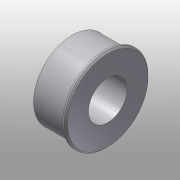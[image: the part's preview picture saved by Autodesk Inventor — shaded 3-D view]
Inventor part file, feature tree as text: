
AUTODESK INVENTOR PART (.ipt)
format: ipt  version: 2016 (Build 200138000, 138)  size: 109,056 bytes
history: native  units: mm
features: extrude x3, sketch x3, chamfer x1
ambient origin geometry x8: Origin, YZ Plane, XZ Plane, XY Plane, X Axis, Y Axis, Z Axis, Center Point
bodies: Solid1 (feature_tree)
feature tree (7):
  extrude  "Extrusion1"  Depth=5.0mm TaperAngle=0.0deg
  extrude  "Extrusion2"  Depth=0.5mm TaperAngle=0.0deg
  chamfer  "Chamfer1"  Distance=0.25mm Angle=45.0deg
  extrude  "Extrusion3"  Depth=5.0mm TaperAngle=0.0deg
  sketch  "Sketch1"  dims[d0=12.0mm d1=5.0mm d2=0.0mm]
  sketch  "Sketch2"  dims[d3=13.0mm d4=0.5mm d5=0.0mm d6=0.25mm d7=2.0mm d8=45.0deg]
  sketch  "Sketch3"  dims[d9=6.0mm d10=5.0mm d11=0.0mm]
